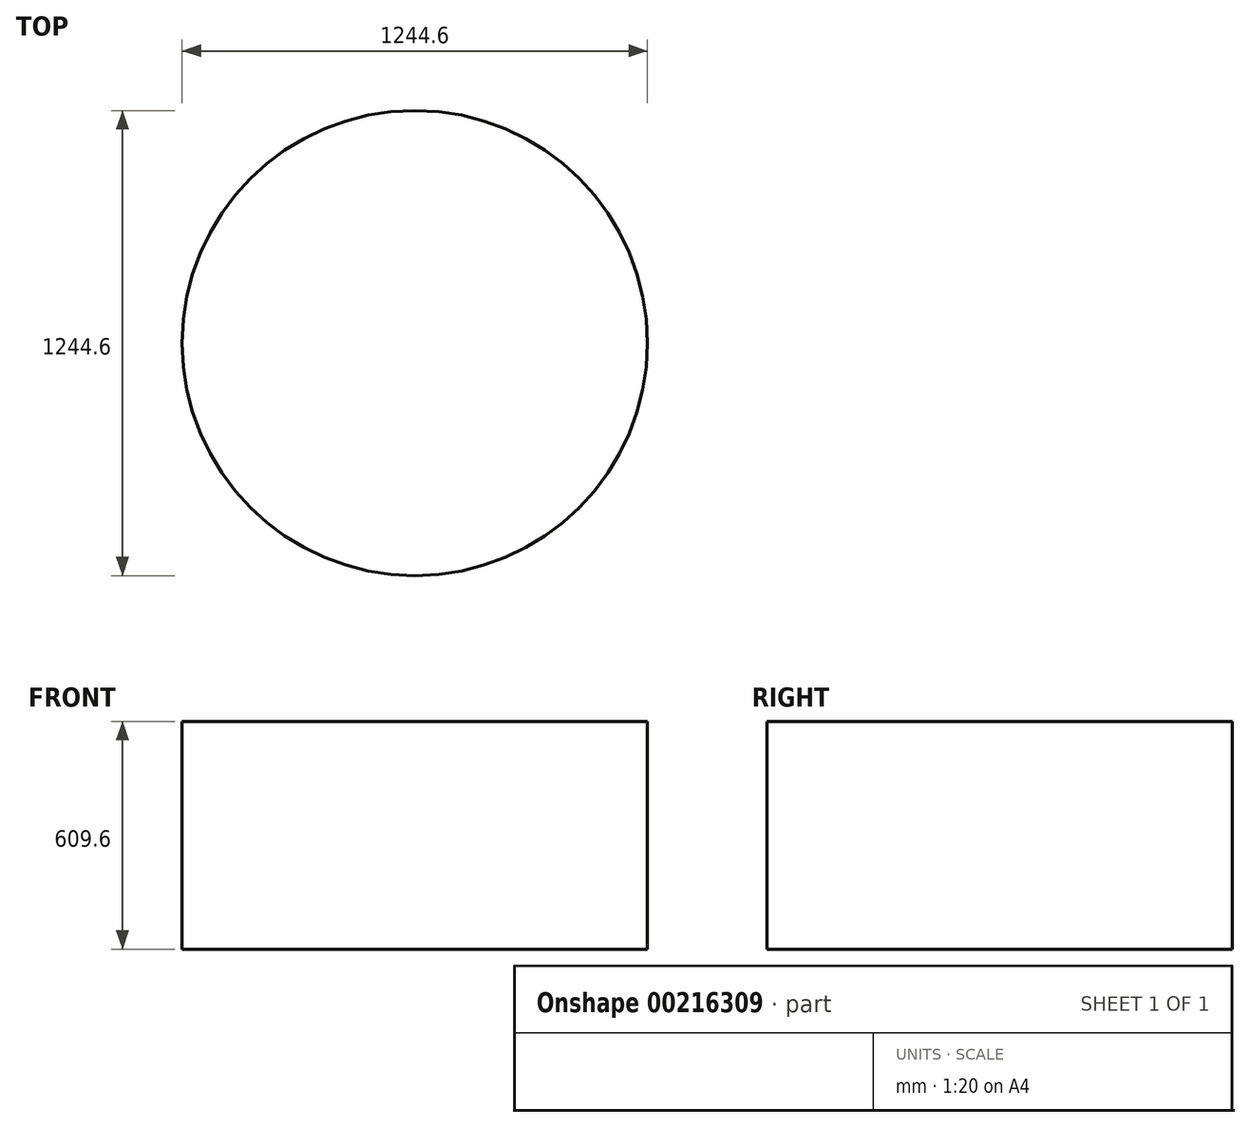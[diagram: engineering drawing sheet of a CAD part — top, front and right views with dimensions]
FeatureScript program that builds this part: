
annotation { "Feature Type Name" : "Feature", "Feature Type Description" : "" }
export const myFeature = defineFeature(function(context is Context, id is Id, definition is map)
    precondition{}
    {
        {
            var Q0;
            Q0=qCreatedBy(makeId("Top.planeOp"),FACE);
            var sketch = newSketch(context, id + "F0", { "sketchPlane" : qUnion([Q0])});
            skCircle(sketch, "E0", {"center": v(0, 0) * mm, "radius": 622.3 * mm});
            skSolve(sketch);
        }
        {
            var Q0;
            Q0=makeQuery(id+"F0.imprint","IMPRINT",FACE,{"disambiguationData":[TD([[makeQuery(id+"F0.imprint","IMPRINT",EDGE,{"derivedFrom":sQuery(id+"F0.wireOp",EDGE,"E0")}),1.0]])]});
            extrude(context, id + "F1", {"entities" : qUnion([Q0]), "oppositeDirection" : true, "depth" : 609.6 * mm});
        }
    });
